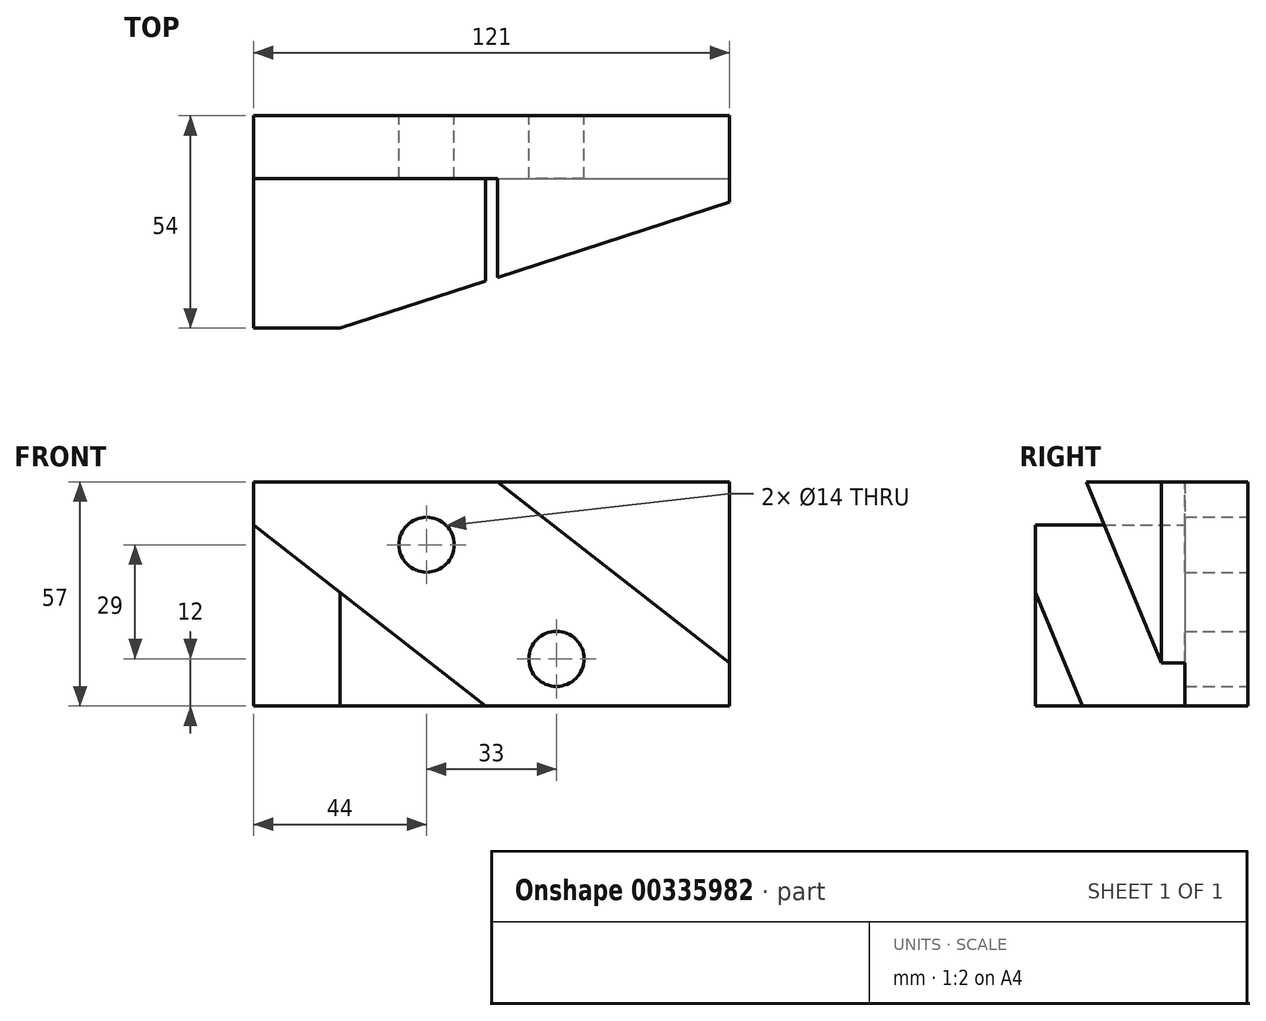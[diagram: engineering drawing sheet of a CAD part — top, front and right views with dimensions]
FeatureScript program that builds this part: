
annotation { "Feature Type Name" : "Feature", "Feature Type Description" : "" }
export const myFeature = defineFeature(function(context is Context, id is Id, definition is map)
    precondition{}
    {
        {
            var Q0;
            Q0=qCreatedBy(makeId("Front.planeOp"),FACE);
            var sketch = newSketch(context, id + "F0", { "sketchPlane" : qUnion([Q0])});
            skLineSegment(sketch, "E0.bottom", {"start": v(0, 0) * mm, "end": v(121, 0) * mm});
            skLineSegment(sketch, "E0.top", {"start": v(0, 57) * mm, "end": v(121, 57) * mm});
            skLineSegment(sketch, "E0.left", {"start": v(0, 0) * mm, "end": v(0, 57) * mm});
            skLineSegment(sketch, "E0.right", {"start": v(121, 0) * mm, "end": v(121, 57) * mm});
            skLineSegment(sketch, "E1", {"start": v(62, 57) * mm, "end": v(121, 11) * mm});
            skLineSegment(sketch, "E2", {"start": v(0, 46) * mm, "end": v(59, 0) * mm});
            skCircle(sketch, "E3", {"center": v(44, 41) * mm, "radius": 7 * mm});
            skCircle(sketch, "E4", {"center": v(77, 12) * mm, "radius": 7 * mm});
            skSolve(sketch);
        }
        {
            var Q0;
            {var subQ4=sQuery(id+"F0.wireOp",EDGE,"E1");Q0=makeQuery(id+"F0.imprint","IMPRINT",FACE,{"disambiguationData":[TD([[makeQuery(id+"F0.imprint","IMPRINT",EDGE,{"derivedFrom":subQ4}),-1.0]])]});}
            extrude(context, id + "F1", {"entities" : qUnion([Q0]), "depth" : 16 * mm});
        }
        {
            var Q0;
            {var subQ3=sQuery(id+"F0.wireOp",EDGE,"E2");Q0=makeQuery(id+"F0.imprint","IMPRINT",FACE,{"disambiguationData":[TD([[makeQuery(id+"F0.imprint","IMPRINT",EDGE,{"derivedFrom":subQ3}),-1.0]])]});}
            var Q1;
            {var subQ3=sQuery(id+"F0.wireOp",EDGE,"E1");Q1=makeQuery(id+"F0.imprint","IMPRINT",FACE,{"disambiguationData":[TD([[makeQuery(id+"F0.imprint","IMPRINT",EDGE,{"derivedFrom":subQ3}),1.0]])]});}
            extrude(context, id + "F2", {"entities" : qUnion([Q0, Q1]), "operationType" : NewBodyOperationType.ADD, "depth" : 54 * mm});
        }
        {
            var Q0;
            {var subQ0=sQuery(id+"F0.wireOp",EDGE,"E0.top");Q0=makeQuery(id+"F2.boolean.opBoolean","MERGE",FACE,{"derivedFrom":[makeQuery(id+"F1.opExtrude","SWEPT_FACE",FACE,{"disambiguationData":[OSD([subQ0])]}),makeQuery(id+"F2.opExtrude","SWEPT_FACE",FACE,{"disambiguationData":[OSD([subQ0])]})]});}
            var sketch = newSketch(context, id + "F3", { "sketchPlane" : qUnion([Q0])});
            skLineSegment(sketch, "E5.0", {"start": v(0, -54) * mm, "end": v(59, -54) * mm});
            skLineSegment(sketch, "E6", {"start": v(121, 0) * mm, "end": v(121, -22) * mm});
            skLineSegment(sketch, "E7", {"start": v(0, -54) * mm, "end": v(22, -54) * mm});
            skLineSegment(sketch, "E8", {"start": v(22, -54) * mm, "end": v(121, -22) * mm});
            skSolve(sketch);
        }
        {
            var Q0;
            Q0 = qSketchRegion(id + "F3", true);
            var Q1;
            {var subQ1=sQuery(id+"F0.wireOp",EDGE,"E0.top");var subQ6=makeQuery(id+"F2.opExtrude","CAP_EDGE",EDGE,{"disambiguationData":[OSD([subQ1])],"isStart":false});Q1=makeQuery(id+"F3.imprint","IMPRINT",FACE,{"disambiguationData":[TD([[makeQuery(id+"F3.imprint","IMPRINT",EDGE,{"derivedFrom":subQ6}),1.0]])]});}
            extrude(context, id + "F4", {"entities" : qUnion([Q0, Q1]), "operationType" : NewBodyOperationType.REMOVE, "endBound" : BoundingType.THROUGH_ALL, "oppositeDirection" : true, "depth" : 25 * mm});
        }
        {
            var Q0;
            {var subQ0=sQuery(id+"F0.wireOp",EDGE,"E0.bottom");Q0=makeQuery(id+"F2.boolean.opBoolean","MERGE",FACE,{"derivedFrom":[makeQuery(id+"F1.opExtrude","SWEPT_FACE",FACE,{"disambiguationData":[OSD([subQ0])]}),makeQuery(id+"F2.opExtrude","SWEPT_FACE",FACE,{"disambiguationData":[OSD([subQ0])]})]});}
            var sketch = newSketch(context, id + "F5", { "sketchPlane" : qUnion([Q0])});
            skLineSegment(sketch, "E9.0", {"start": v(62, 41.07) * mm, "end": v(121, 22) * mm});
            skLineSegment(sketch, "E10", {"start": v(0, 54) * mm, "end": v(22, 54) * mm});
            skLineSegment(sketch, "E11", {"start": v(62, 41.07) * mm, "end": v(22, 54) * mm});
            skSolve(sketch);
        }
        {
            var Q0;
            Q0 = qSketchRegion(id + "F5", true);
            var Q1;
            {var subQ0=sQuery(id+"F5.wireOp",EDGE,"E11");var subQ1=sQuery(id+"F0.wireOp",EDGE,"E0.bottom");var subQ2=makeQuery(id+"F2.opExtrude","CAP_EDGE",EDGE,{"disambiguationData":[OSD([subQ1])],"isStart":false});var subQ3=makeQuery(id+"F5.imprint","INTERSECT",VERTEX,{"derivedFrom":[subQ2,sQuery(id+"F5.wireOp",EDGE,"E10"),subQ0]});Q1=makeQuery(id+"F5.imprint","IMPRINT",FACE,{"disambiguationData":[TD([[makeQuery(id+"F5.imprint","IMPRINT",EDGE,{"disambiguationData":[TD([[subQ3,1.0]])],"derivedFrom":subQ0}),-1.0]])]});}
            extrude(context, id + "F6", {"entities" : qUnion([Q0, Q1]), "operationType" : NewBodyOperationType.REMOVE, "endBound" : BoundingType.THROUGH_ALL, "oppositeDirection" : true, "depth" : 25 * mm});
        }
    });
